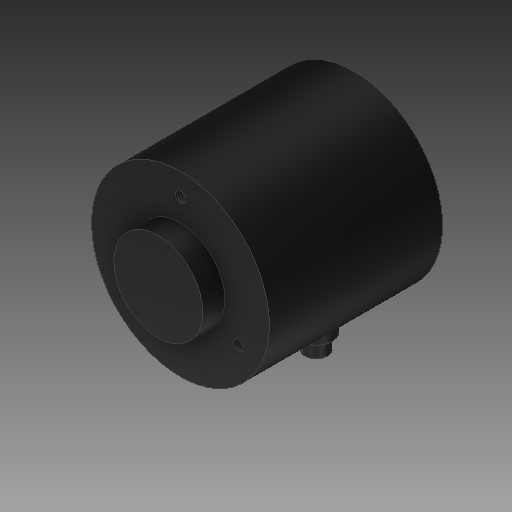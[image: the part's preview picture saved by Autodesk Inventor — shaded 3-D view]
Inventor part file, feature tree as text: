
AUTODESK INVENTOR PART (.ipt)
format: ipt  version: 2018 (Build 220112000, 112)  size: 152,576 bytes
history: native  units: mm
features: sketch x5, extrude x4, hole x1, plane x1, projected_geometry x1
ambient origin geometry x8: Origin, YZ Plane, XZ Plane, XY Plane, X Axis, Y Axis, Z Axis, Center Point
bodies: Solid1 (feature_tree)
feature tree (12):
  extrude  "Extrusion1"  Depth=39.0mm TaperAngle=0.0deg
  extrude  "Extrusion2"  Depth=20.0mm TaperAngle=0.0deg
  hole  "Hole1"  [1 undecoded]
  plane  "Work Plane2"
  extrude  "Extrusion6"  Depth=7.3mm
  extrude  "Extrusion7"  Depth=10.0mm
  sketch  "Sketch1"  dims[d0=40.0mm d1=39.0mm d2=0.0mm]
  sketch  "Sketch2"  dims[d3=20.0mm d4=5.0mm d5=0.0mm]
  sketch  "Sketch3"  dims[d6=30.0mm d7=30.0mm d9=360.0deg]
  sketch  "Sketch6"  dims[d11=2.459mm d12=7.0mm d13=4.0mm d14=2.0mm d15=90.0deg d16=9.8mm d17=20.594885mm d25=7.3mm]
  projected_geometry  "Projected Loop2"
  sketch  "Sketch7"  dims[d26=8.47mm d29=0.9mm d30=6.58mm d31=0.0mm d32=5.1mm d33=10.0mm d34=0.0mm d35=3.29mm d36=0.0mm]
note: 1 required parameter value undecoded (feature->parameter linkage not recoverable at this tier; creation-order binding heuristic only, values carry confidence <= 0.55)
